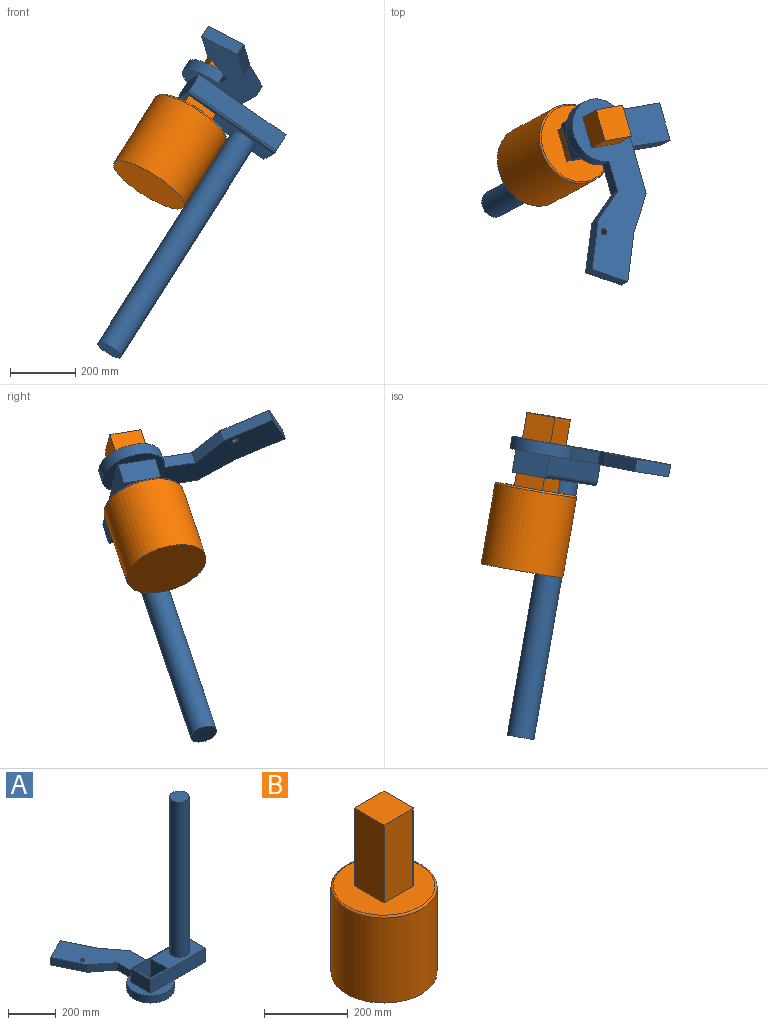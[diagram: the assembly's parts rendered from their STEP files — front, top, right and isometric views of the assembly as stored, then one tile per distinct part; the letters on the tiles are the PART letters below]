
ASSEMBLY  parts=2 mates=1
PART A: 24 faces, bbox 439.3x580.6x907.7 mm
  f0: plane 580.58x271.84mm, normal (0,0,-1), area 69374.9mm2, adj f4,f5,f6,f7,f10,f11,f12,f13
  f1: plane 327.5x59.75mm, normal (0,1,0), area 19569.3mm2, adj f2,f9,f19,f20,f23
  f2: plane 120x69.75mm, normal (-1,0,0), area 8348.9mm2, adj f1,f3,f8,f9,f23
  f3: plane 327.5x69.75mm, normal (0,-1,0), area 22844.3mm2, adj f2,f8,f9,f19,f20
  f4: plane 108.03x100mm, normal (1,0,0), area 10802.8mm2, adj f0,f5,f7,f8
  f5: plane 108.03x100mm, normal (0,-1,0), area 10802.8mm2, adj f0,f4,f6,f23
  f6: plane 108.03x100mm, normal (-1,0,0), area 10802.8mm2, adj f0,f5,f7,f8
  f7: plane 108.03x100mm, normal (0,1,0), area 10802.8mm2, adj f0,f4,f6,f8
  f8: plane 327.5x110mm, normal (0,0,1), area 20665.9mm2, adj f2,f3,f4,f6,f7,f20,f21,f23
  f9: plane 580.58x271.84mm, normal (0,0,1), area 60557.4mm2, adj f1,f2,f3,f10,f11,f12,f13,f14
  f10: plane 99.08x76.67mm, normal (-0.61,-0.79,0), area 4795.1mm2, adj f0,f9,f14,f15
  f11: plane 111.48x83.04mm, normal (0.8,0.6,0), area 5320.5mm2, adj f0,f9,f12,f16
  f12: plane 220.22x38.28mm, normal (1,0,0), area 8428.9mm2, adj f0,f9,f11,f13,f19
  f13: cylinder r=100mm len=200mm, axis (0,0,-1), area 17992.4mm2, adj f0,f9,f12,f14,f19
  f14: plane 98.32x38.28mm, normal (-1,0.01,0), area 3763.6mm2, adj f0,f9,f10,f13
  f15: plane 148.89x72.76mm, normal (-0.9,-0.44,0), area 6342.8mm2, adj f0,f9,f10,f17
  f16: plane 148.89x72.76mm, normal (0.9,0.44,0), area 6342.8mm2, adj f0,f9,f11,f17
  f17: plane 116.04x56.71mm, normal (-0.44,0.9,0), area 4943.3mm2, adj f0,f9,f15,f16
  f18: cylinder r=10mm len=38.28mm, axis (0,0,1), area 2404.9mm2, adj f0,f9
  f19: plane 187.5x120mm, normal (0,0,-1), area 20483mm2, adj f1,f3,f12,f13,f20
  f20: plane 120x69.75mm, normal (1,0,0), area 8348.9mm2, adj f1,f3,f8,f19,f23
  f21: cylinder r=41.3mm len=799.67mm, axis (0,0,-1), area 207531mm2, adj f8,f22
  f22: plane 82.61x82.61mm, normal (0,0,1), area 5359.6mm2, adj f21
  f23: cylinder r=10mm len=327.5mm, axis (1,0,0), area 5144.4mm2, adj f1,f2,f5,f8,f20
PART B: 11 faces, bbox 274.9x274.9x481.9 mm
  f0: cylinder r=127mm len=254mm, axis (0,0,-1), area 198693.2mm2, adj f2,f3
  f1: plane 244x244mm, normal (0,0,1), area 36760.9mm2, adj f3,f4,f5,f6,f7,f8,f9
  f2: plane 254x254mm, normal (0,0,-1), area 50670.7mm2, adj f0
  f3: torus R=122mm, axis (0,0,1), area 6177.5mm2, adj f0,f1
  f4: plane 227.91x0.35mm, normal (1,0,0), area 79.3mm2, adj f1,f5,f9,f10
  f5: plane 227.91x4.15mm, normal (0,-1,0), area 945.6mm2, adj f1,f4,f6,f10
  f6: plane 227.91x99.65mm, normal (1,0,0), area 22711.7mm2, adj f1,f5,f7,f10
  f7: plane 227.91x100mm, normal (0,1,0), area 22791mm2, adj f1,f6,f8,f10
  f8: plane 227.91x100mm, normal (-1,0,0), area 22791mm2, adj f1,f7,f9,f10
  f9: plane 227.91x95.85mm, normal (0,-1,0), area 21845.4mm2, adj f1,f4,f8,f10
  f10: plane 100x100mm, normal (0,0,1), area 9998.6mm2, adj f4,f5,f6,f7,f8,f9
PLACE A rot(axis=(0.95,0.11,-0.29),167deg) t=(119.24,-1.35,582.41)mm
PLACE B rot(axis=(-0.29,-0.11,-0.95),167.6deg) t=(-87.77,-112.03,256.28)mm fixed
MATE planar A.f5 <-> B.f7  axis (-0.27,0.95,-0.15) through (104.88,-63.78,546.17)mm
